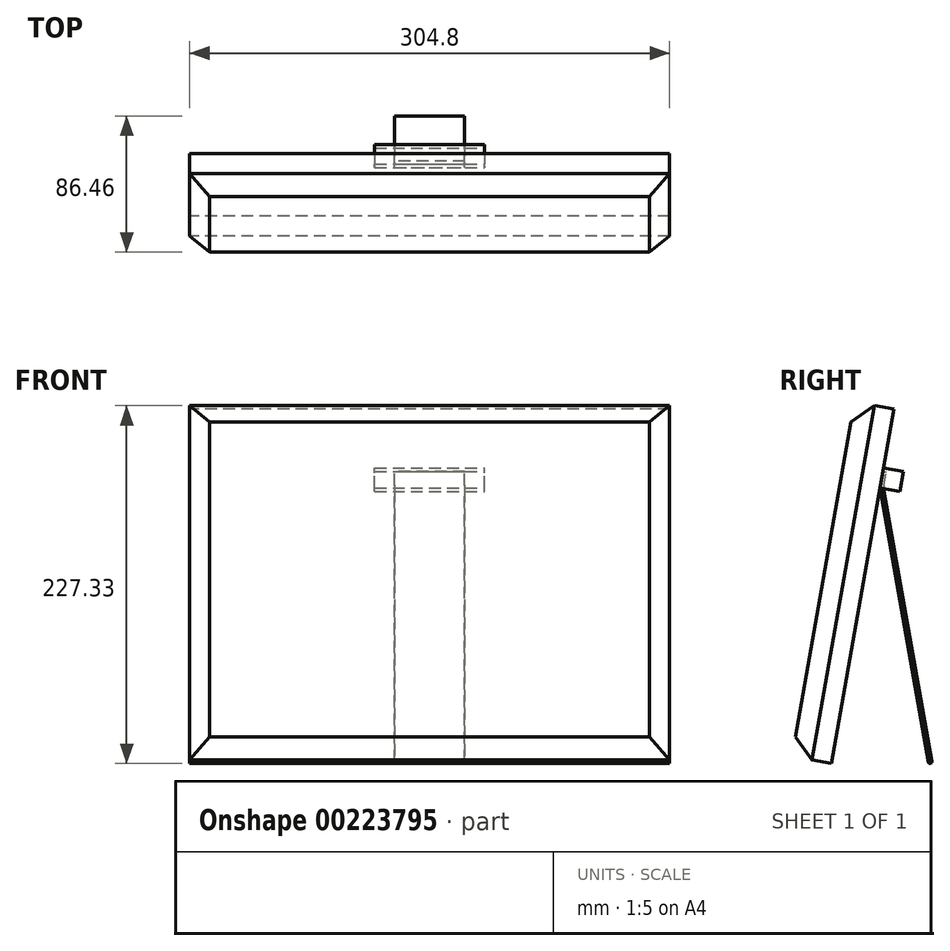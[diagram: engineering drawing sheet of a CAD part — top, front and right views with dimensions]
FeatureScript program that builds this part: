
annotation { "Feature Type Name" : "Feature", "Feature Type Description" : "" }
export const myFeature = defineFeature(function(context is Context, id is Id, definition is map)
    precondition{}
    {
        {
            var Q0;
            Q0=qCreatedBy(makeId("Front.planeOp"),FACE);
            var sketch = newSketch(context, id + "F0", { "sketchPlane" : qUnion([Q0])});
            skLineSegment(sketch, "E0.bottom", {"start": v(152.4, 114.3) * mm, "end": v(-152.4, 114.3) * mm});
            skLineSegment(sketch, "E0.top", {"start": v(152.4, -114.3) * mm, "end": v(-152.4, -114.3) * mm});
            skLineSegment(sketch, "E0.left", {"start": v(152.4, 114.3) * mm, "end": v(152.4, -114.3) * mm});
            skLineSegment(sketch, "E0.right", {"start": v(-152.4, 114.3) * mm, "end": v(-152.4, -114.3) * mm});
            skPoint(sketch, "E0.middle", {"position": v(0, 0) * mm});
            skSolve(sketch);
        }
        {
            var Q0;
            Q0 = qSketchRegion(id + "F0", true);
            extrude(context, id + "F1", {"entities" : qUnion([Q0]), "depth" : 25.4 * mm});
        }
        {
            var Q0;
            Q0=makeQuery(id+"F1.opExtrude","CAP_FACE",FACE,{"disambiguationData":[OSD([sQuery(id+"F0.wireOp",EDGE,"E0.bottom"),sQuery(id+"F0.wireOp",EDGE,"E0.top"),sQuery(id+"F0.wireOp",EDGE,"E0.left"),sQuery(id+"F0.wireOp",EDGE,"E0.right")])],"isStart":false});
            chamfer(context, id + "F2", {"entities" : qUnion([Q0]), "width" : 12.7 * mm, "tangentPropagation" : true});
        }
        {
            var Q0;
            Q0=makeQuery(id+"F1.opExtrude","CAP_FACE",FACE,{"disambiguationData":[OSD([sQuery(id+"F0.wireOp",EDGE,"E0.bottom"),sQuery(id+"F0.wireOp",EDGE,"E0.top"),sQuery(id+"F0.wireOp",EDGE,"E0.left"),sQuery(id+"F0.wireOp",EDGE,"E0.right")])],"isStart":true});
            var sketch = newSketch(context, id + "F3", { "sketchPlane" : qUnion([Q0])});
            skLineSegment(sketch, "E1.bottom", {"start": v(34.92, 63.5) * mm, "end": v(-34.92, 63.5) * mm});
            skLineSegment(sketch, "E1.top", {"start": v(34.92, 76.2) * mm, "end": v(-34.92, 76.2) * mm});
            skLineSegment(sketch, "E1.left", {"start": v(34.93, 63.5) * mm, "end": v(34.92, 76.2) * mm});
            skLineSegment(sketch, "E1.right", {"start": v(-34.92, 63.5) * mm, "end": v(-34.93, 76.2) * mm});
            skPoint(sketch, "E1.middle", {"position": v(0, 69.85) * mm});
            skSolve(sketch);
        }
        {
            var Q0;
            Q0 = qSketchRegion(id + "F3", true);
            extrude(context, id + "F4", {"entities" : qUnion([Q0]), "operationType" : NewBodyOperationType.ADD, "depth" : 12.7 * mm});
        }
        {
            var Q0;
            Q0=makeQuery(id+"F1.opExtrude","SWEPT_BODY",BODY,{"disambiguationData":[OSD([sQuery(id+"F0.wireOp",EDGE,"E0.bottom"),sQuery(id+"F0.wireOp",EDGE,"E0.top"),sQuery(id+"F0.wireOp",EDGE,"E0.left"),sQuery(id+"F0.wireOp",EDGE,"E0.right")])]});
            var Q1;
            Q1=makeQuery(id+"F1.opExtrude","CAP_EDGE",EDGE,{"disambiguationData":[OSD([sQuery(id+"F0.wireOp",EDGE,"E0.top")])],"isStart":true});
            transform(context, id + "F5", {"entities" : qUnion([Q0]), "transformType" : TransformType.ROTATION, "transformAxis" : qUnion([Q1]), "angle" : 10 * degree, "makeCopy" : false});
        }
        {
            var Q0;
            Q0=qCreatedBy(makeId("Right.planeOp"),FACE);
            var sketch = newSketch(context, id + "F6", { "sketchPlane" : qUnion([Q0])});
            skLineSegment(sketch, "E2.0.0", {"start": v(33.08, 73.3) * mm, "end": v(30.87, 60.8) * mm, "construction": true});
            skLineSegment(sketch, "E2.0.1", {"start": v(30.87, 60.8) * mm, "end": v(43.38, 58.6) * mm, "construction": true});
            skLineSegment(sketch, "E2.0.2", {"start": v(43.38, 58.6) * mm, "end": v(45.59, 71.1) * mm, "construction": true});
            skLineSegment(sketch, "E2.0.3", {"start": v(45.59, 71.1) * mm, "end": v(33.08, 73.3) * mm, "construction": true});
            skPoint(sketch, "E3.0", {"position": v(0, -114.3) * mm});
            skLineSegment(sketch, "E4.0", {"start": v(39.7, 110.83) * mm, "end": v(0, -114.3) * mm, "construction": true});
            skLineSegment(sketch, "E5.0", {"start": v(33.42, 62.58) * mm, "end": v(31.26, 62.97) * mm});
            skLineSegment(sketch, "E5.1", {"start": v(33.42, 62.58) * mm, "end": v(34.86, 70.76) * mm});
            skLineSegment(sketch, "E5.2", {"start": v(32.7, 71.14) * mm, "end": v(34.86, 70.76) * mm});
            skLineSegment(sketch, "E6", {"start": v(34.86, 70.76) * mm, "end": v(33.04, 60.42) * mm});
            skLineSegment(sketch, "E7", {"start": v(33.04, 60.42) * mm, "end": v(30.87, 60.8) * mm});
            skLineSegment(sketch, "E8", {"start": v(30.87, 60.8) * mm, "end": v(32.7, 71.14) * mm});
            skLineSegment(sketch, "E9", {"start": v(32.7, 71.14) * mm, "end": v(31.26, 62.97) * mm});
            skLineSegment(sketch, "E10", {"start": v(30.87, 60.8) * mm, "end": v(61.6, -113.45) * mm});
            skLineSegment(sketch, "E11", {"start": v(61.6, -113.45) * mm, "end": v(63.63, -113.09) * mm});
            skLineSegment(sketch, "E12", {"start": v(63.63, -113.09) * mm, "end": v(33.04, 60.42) * mm});
            skArc(sketch, "E13", {"start": v(61.6, -113.45) * mm, "mid": v(62.8, -114.28) * mm, "end": v(63.63, -113.09) * mm});
            skLineSegment(sketch, "E14", {"start": v(0, -114.3) * mm, "end": v(62.62, -114.3) * mm, "construction": true});
            skSolve(sketch);
        }
        {
            var Q0;
            Q0 = qSketchRegion(id + "F6", true);
            extrude(context, id + "F7", {"entities" : qUnion([Q0]), "endBound" : BoundingType.SYMMETRIC, "depth" : 44.45 * mm});
        }
        {
            var Q0;
            Q0=makeQuery(id+"F7.opExtrude","SWEPT_EDGE",EDGE,{"disambiguationData":[OSD([sQuery(id+"F6.wireOp",EDGE,"E6"),sQuery(id+"F6.wireOp",EDGE,"E7"),sQuery(id+"F6.wireOp",EDGE,"E12")])]});
            var Q1;
            Q1=makeQuery(id+"F7.opExtrude","SWEPT_EDGE",EDGE,{"disambiguationData":[OSD([sQuery(id+"F6.wireOp",EDGE,"E7"),sQuery(id+"F6.wireOp",EDGE,"E8"),sQuery(id+"F6.wireOp",EDGE,"E10")])]});
            fillet(context, id + "F8", {"entities" : qUnion([Q0, Q1]), "radius" : 10 * mm, "tangentPropagation" : true, "allowEdgeOverflow" : false});
        }
    });
